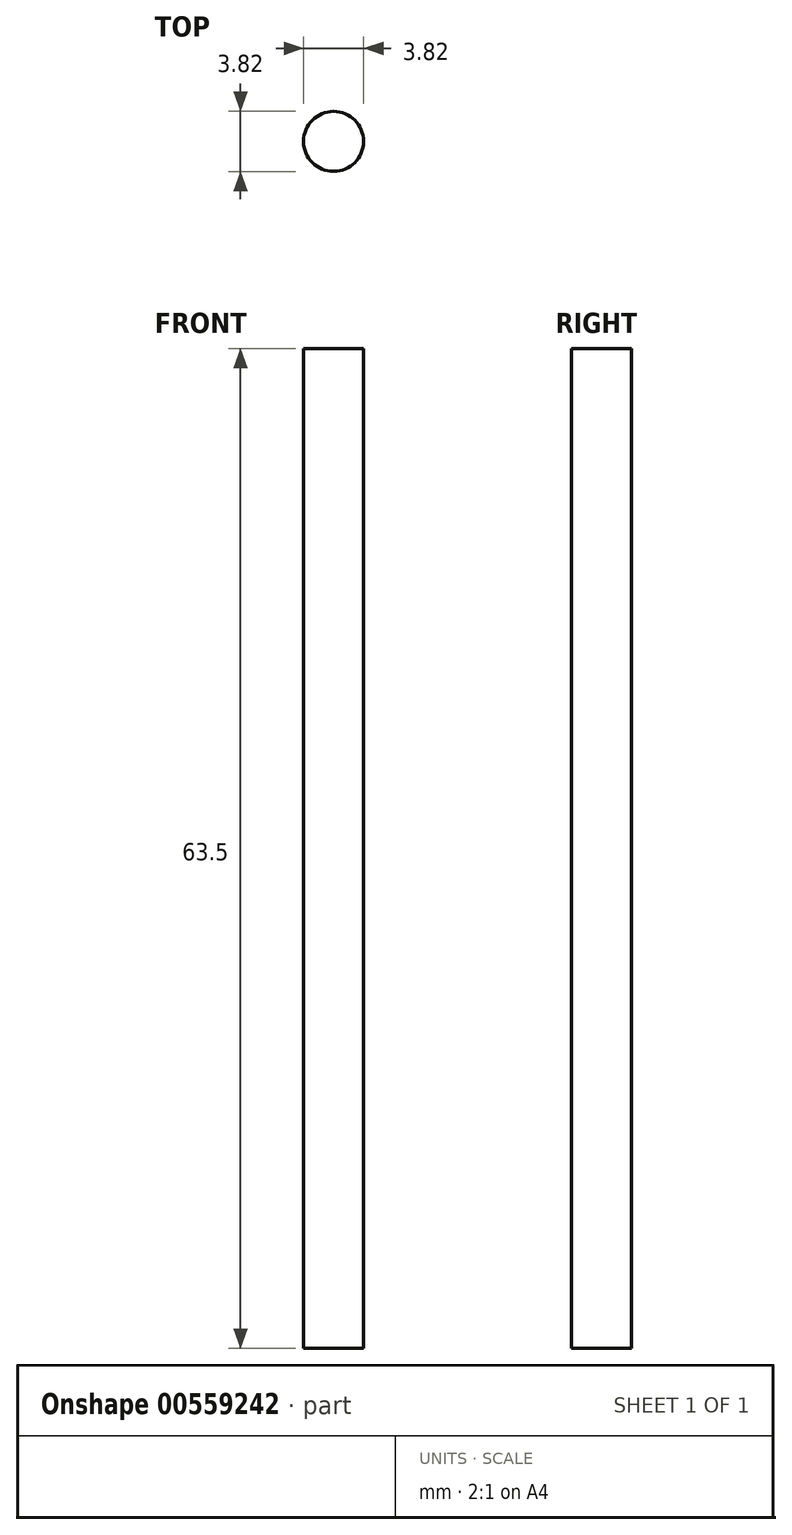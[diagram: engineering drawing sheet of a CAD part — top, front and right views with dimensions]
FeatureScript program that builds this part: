
annotation { "Feature Type Name" : "Feature", "Feature Type Description" : "" }
export const myFeature = defineFeature(function(context is Context, id is Id, definition is map)
    precondition{}
    {
        {
            var Q0;
            Q0=qCreatedBy(makeId("Top.planeOp"),FACE);
            var sketch = newSketch(context, id + "F0", { "sketchPlane" : qUnion([Q0])});
            skCircle(sketch, "E0", {"center": v(0, 0) * mm, "radius": 1.9 * mm});
            skSolve(sketch);
        }
        {
            var Q0;
            Q0=qSketchRegion(id+"F0",true);
            extrude(context, id + "F1", {"entities" : qUnion([Q0]), "depth" : 63.5 * mm, "offsetDistance" : 25.4 * mm});
        }
    });
